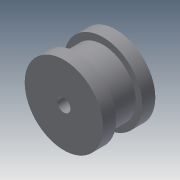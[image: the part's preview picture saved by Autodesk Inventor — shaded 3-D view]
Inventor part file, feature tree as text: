
AUTODESK INVENTOR PART (.ipt)
format: ipt  version: 2015 (Build 190159000, 159)  size: 104,448 bytes
history: native  units: mm
features: extrude x5, sketch x5
ambient origin geometry x8: Origin, YZ Plane, XZ Plane, XY Plane, X Axis, Y Axis, Z Axis, Center Point
bodies: Solid1 (feature_tree)
feature tree (10):
  extrude  "Extrusion1"  Depth=10.0mm TaperAngle=0.0deg
  extrude  "Extrusion2"  Depth=10.0mm TaperAngle=0.0deg
  extrude  "Extrusion3"  Depth=20.0mm TaperAngle=0.0deg
  extrude  "Extrusion4"  Depth=10.0mm TaperAngle=0.0deg
  extrude  "Extrusion5"  Depth=10.0mm TaperAngle=0.0deg
  sketch  "Sketch1"  dims[d0=60.0mm d1=10.0mm d2=0.0mm]
  sketch  "Sketch2"  dims[d3=10.0mm d4=10.0mm d5=0.0mm]
  sketch  "Sketch3"  dims[d6=50.0mm d7=20.0mm d8=0.0mm]
  sketch  "Sketch5"  dims[d9=60.0mm d10=10.0mm d11=0.0mm]
  sketch  "Sketch6"  dims[d12=10.0mm d13=10.0mm d14=0.0mm]
